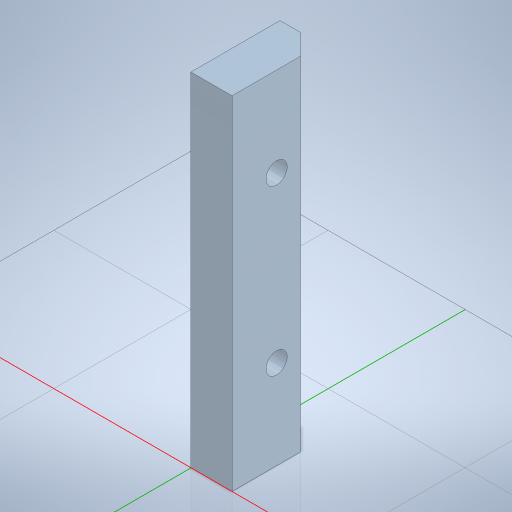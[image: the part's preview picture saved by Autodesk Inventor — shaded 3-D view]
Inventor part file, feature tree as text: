
AUTODESK INVENTOR PART (.ipt)
format: ipt  version: 2024 (Build 280153000, 153)  size: 283,648 bytes
history: native  units: mm
features: sketch x2, extrude x1, hole x1
ambient origin geometry x8: Origin, YZ Plane, XZ Plane, XY Plane, X Axis, Y Axis, Z Axis, Center Point
bodies: Volumenkörper1 (feature_tree)
feature tree (4):
  extrude  "Extrusion1"  Depth=13.0mm
  hole  "Bohrung1"  [1 undecoded]
  sketch  "Skizze1"  dims[d0=6.0mm d1=13.0mm]
  sketch  "Skizze2"  dims[d2=3.0mm d3=45.0deg d4=50.0mm d5=0.0mm d6=3.1mm d7=5.0mm d8=4.0mm d9=2.0mm d10=90.0deg d11=8.0mm d12=0.0mm d13=24.0mm d14=13.0mm]
note: 1 required parameter value undecoded (feature->parameter linkage not recoverable at this tier; creation-order binding heuristic only, values carry confidence <= 0.55)
